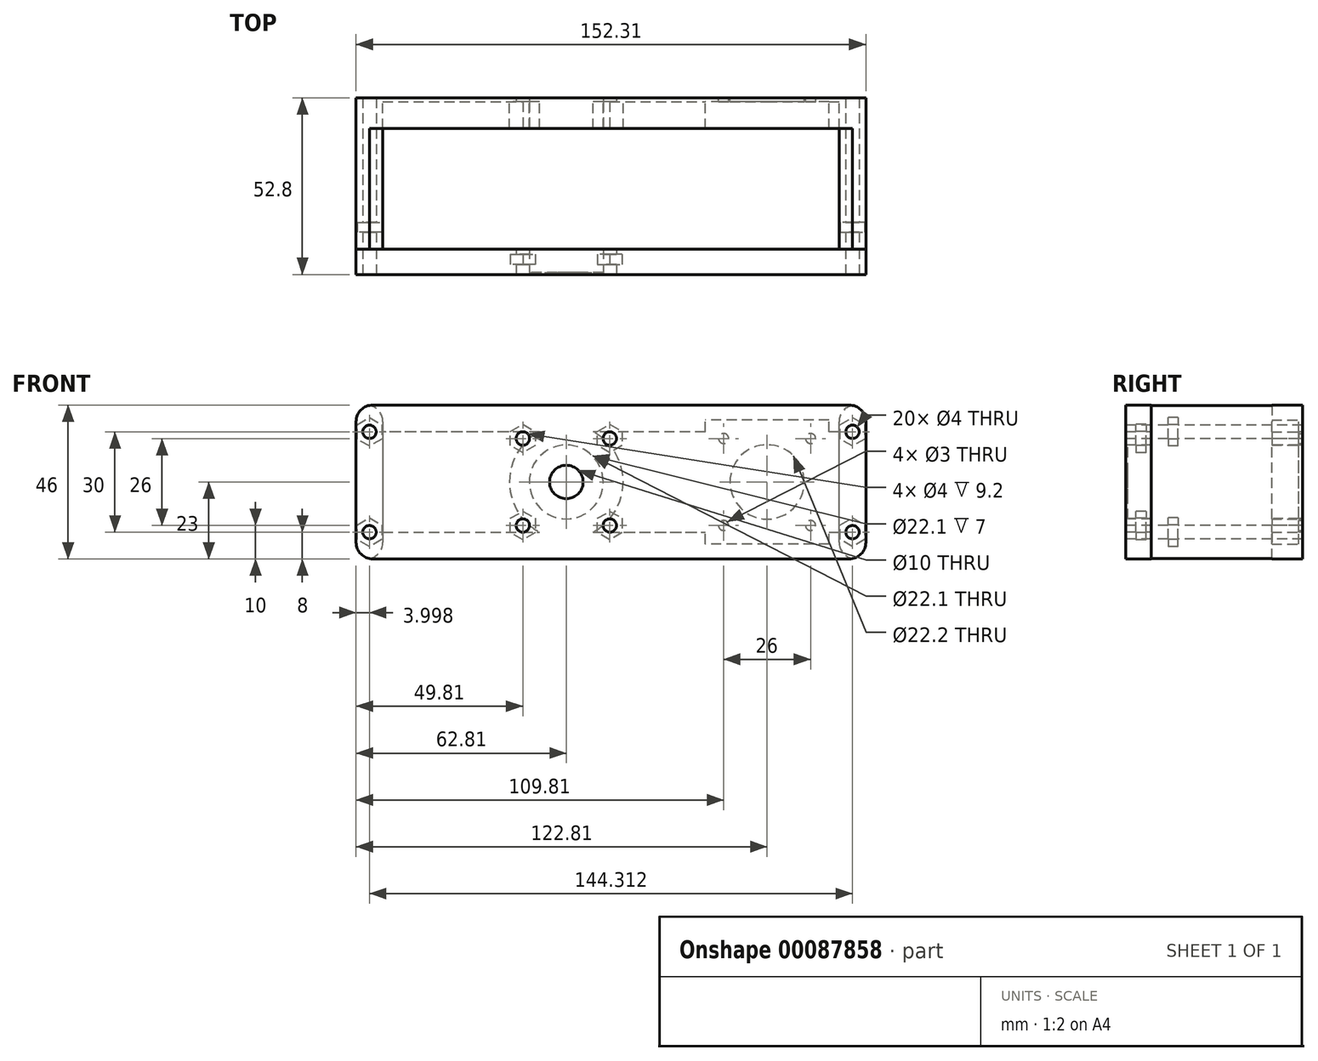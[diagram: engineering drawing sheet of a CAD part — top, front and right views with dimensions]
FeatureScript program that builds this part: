
annotation { "Feature Type Name" : "Feature", "Feature Type Description" : "" }
export const myFeature = defineFeature(function(context is Context, id is Id, definition is map)
    precondition{}
    {
        {
            var Q0;
            Q0=qCreatedBy(makeId("Front.planeOp"),FACE);
            var sketch = newSketch(context, id + "F0", { "sketchPlane" : qUnion([Q0])});
            skCircle(sketch, "E0", {"center": v(0, 0) * mm, "radius": 11.05 * mm});
            skCircle(sketch, "E1", {"center": v(60, 0) * mm, "radius": 11.1 * mm});
            skLineSegment(sketch, "E2.bottom", {"start": v(73, -13) * mm, "end": v(47, -13) * mm, "construction": true});
            skLineSegment(sketch, "E2.top", {"start": v(73, 13) * mm, "end": v(47, 13) * mm, "construction": true});
            skLineSegment(sketch, "E2.left", {"start": v(73, -13) * mm, "end": v(73, 13) * mm, "construction": true});
            skLineSegment(sketch, "E2.right", {"start": v(47, -13) * mm, "end": v(47, 13) * mm, "construction": true});
            skCircle(sketch, "E3", {"center": v(47, 13) * mm, "radius": 1.5 * mm});
            skCircle(sketch, "E4", {"center": v(73, 13) * mm, "radius": 1.5 * mm});
            skCircle(sketch, "E5", {"center": v(73, -13) * mm, "radius": 1.5 * mm});
            skCircle(sketch, "E6", {"center": v(47, -13) * mm, "radius": 1.5 * mm});
            skLineSegment(sketch, "E7.bottom", {"start": v(-62.81, 23) * mm, "end": v(89.5, 23) * mm});
            skLineSegment(sketch, "E7.top", {"start": v(-62.81, -23) * mm, "end": v(89.5, -23) * mm});
            skLineSegment(sketch, "E7.left", {"start": v(-62.81, 23) * mm, "end": v(-62.81, -23) * mm});
            skLineSegment(sketch, "E7.right", {"start": v(89.5, 23) * mm, "end": v(89.5, -23) * mm});
            skCircle(sketch, "E8", {"center": v(0, 0) * mm, "radius": 47.81 * mm, "construction": true});
            skCircle(sketch, "E9", {"center": v(60, 0) * mm, "radius": 12.19 * mm, "construction": true});
            skCircle(sketch, "E10", {"center": v(0, 0) * mm, "radius": 5 * mm});
            skSolve(sketch);
        }
        {
            var Q0;
            Q0=makeQuery(id+"F0.imprint","IMPRINT",FACE,{"disambiguationData":[TD([[makeQuery(id+"F0.imprint","IMPRINT",EDGE,{"derivedFrom":sQuery(id+"F0.wireOp",EDGE,"E0")}),-1.0]])]});
            extrude(context, id + "F1", {"entities" : qUnion([Q0]), "depth" : 1.2 * mm});
        }
        {
            var Q0;
            Q0=makeQuery(id+"F1.opExtrude","CAP_FACE",FACE,{"disambiguationData":[OSD([sQuery(id+"F0.wireOp",EDGE,"E0"),sQuery(id+"F0.wireOp",EDGE,"E1"),sQuery(id+"F0.wireOp",EDGE,"E3"),sQuery(id+"F0.wireOp",EDGE,"E4"),sQuery(id+"F0.wireOp",EDGE,"E5"),sQuery(id+"F0.wireOp",EDGE,"E6"),sQuery(id+"F0.wireOp",EDGE,"E7.bottom"),sQuery(id+"F0.wireOp",EDGE,"E7.top"),sQuery(id+"F0.wireOp",EDGE,"E7.left"),sQuery(id+"F0.wireOp",EDGE,"E7.right")])],"isStart":false});
            var sketch = newSketch(context, id + "F2", { "sketchPlane" : qUnion([Q0])});
            skLineSegment(sketch, "E11.0", {"start": v(81.5, 15) * mm, "end": v(78.5, 15) * mm});
            skLineSegment(sketch, "E11.1", {"start": v(81.5, -15) * mm, "end": v(81.5, 15) * mm});
            skLineSegment(sketch, "E11.2", {"start": v(-54.81, -15) * mm, "end": v(-8, -15) * mm});
            skLineSegment(sketch, "E11.3", {"start": v(-54.81, 15) * mm, "end": v(-54.81, -15) * mm});
            skArc(sketch, "E12", {"start": v(8, -15) * mm, "mid": v(17, 0) * mm, "end": v(8, 15) * mm});
            skLineSegment(sketch, "E13.trimOffspring", {"start": v(8, -15) * mm, "end": v(41.5, -15) * mm});
            skLineSegment(sketch, "E14.trimOffspring", {"start": v(-8, 15) * mm, "end": v(-54.81, 15) * mm});
            skArc(sketch, "E15.trimOffspring", {"start": v(-8, 15) * mm, "mid": v(-17, 0) * mm, "end": v(-8, -15) * mm});
            skLineSegment(sketch, "E16.bottom", {"start": v(78.5, -18.5) * mm, "end": v(41.5, -18.5) * mm});
            skLineSegment(sketch, "E16.top", {"start": v(78.5, 18.5) * mm, "end": v(41.5, 18.5) * mm});
            skLineSegment(sketch, "E16.left", {"start": v(78.5, -18.5) * mm, "end": v(78.5, 18.5) * mm});
            skLineSegment(sketch, "E16.right", {"start": v(41.5, -18.5) * mm, "end": v(41.5, 18.5) * mm});
            skPoint(sketch, "E16.middle", {"position": v(60, 0) * mm});
            skLineSegment(sketch, "E17.trimOffspring", {"start": v(41.5, 15) * mm, "end": v(8, 15) * mm});
            skLineSegment(sketch, "E18.trimOffspring", {"start": v(78.5, -15) * mm, "end": v(81.5, -15) * mm});
            skSolve(sketch);
        }
        {
            var Q0;
            Q0=makeQuery(id+"F2.imprint","IMPRINT",FACE,{"disambiguationData":[TD([[makeQuery(id+"F2.imprint","IMPRINT",EDGE,{"derivedFrom":sQuery(id+"F2.wireOp",EDGE,"E11.0")}),-1.0]])]});
            extrude(context, id + "F3", {"entities" : qUnion([Q0]), "operationType" : NewBodyOperationType.ADD, "depth" : 8 * mm});
        }
        {
            var Q0;
            Q0=makeQuery(id+"F3.opExtrude","CAP_FACE",FACE,{"disambiguationData":[OSD([sQuery(id+"F0.wireOp",EDGE,"E0"),sQuery(id+"F0.wireOp",EDGE,"E7.bottom"),sQuery(id+"F0.wireOp",EDGE,"E7.top"),sQuery(id+"F0.wireOp",EDGE,"E7.left"),sQuery(id+"F0.wireOp",EDGE,"E7.right"),sQuery(id+"F2.wireOp",EDGE,"E11.0"),sQuery(id+"F2.wireOp",EDGE,"E11.1"),sQuery(id+"F2.wireOp",EDGE,"E11.2"),sQuery(id+"F2.wireOp",EDGE,"E11.3"),sQuery(id+"F2.wireOp",EDGE,"E12"),sQuery(id+"F2.wireOp",EDGE,"E13.trimOffspring"),sQuery(id+"F2.wireOp",EDGE,"E14.trimOffspring"),sQuery(id+"F2.wireOp",EDGE,"E15.trimOffspring")])],"isStart":false});
            var sketch = newSketch(context, id + "F4", { "sketchPlane" : qUnion([Q0])});
            skLineSegment(sketch, "E19.bottom", {"start": v(89.5, -23) * mm, "end": v(81.5, -23) * mm});
            skLineSegment(sketch, "E19.top", {"start": v(89.5, 23) * mm, "end": v(81.5, 23) * mm});
            skLineSegment(sketch, "E19.left", {"start": v(89.5, -23) * mm, "end": v(89.5, 23) * mm});
            skLineSegment(sketch, "E19.right", {"start": v(81.5, -23) * mm, "end": v(81.5, 23) * mm});
            skLineSegment(sketch, "E20.bottom", {"start": v(-62.81, -23) * mm, "end": v(-54.81, -23) * mm});
            skLineSegment(sketch, "E20.top", {"start": v(-62.81, 23) * mm, "end": v(-54.81, 23) * mm});
            skLineSegment(sketch, "E20.left", {"start": v(-62.81, -23) * mm, "end": v(-62.81, 23) * mm});
            skLineSegment(sketch, "E20.right", {"start": v(-54.81, -23) * mm, "end": v(-54.81, 23) * mm});
            skSolve(sketch);
        }
        {
            var Q0;
            Q0 = qSketchRegion(id + "F4", true);
            extrude(context, id + "F5", {"entities" : qUnion([Q0]), "operationType" : NewBodyOperationType.ADD, "depth" : 36 * mm});
        }
        {
            var Q0;
            Q0=makeQuery(id+"F5.opExtrude","CAP_FACE",FACE,{"disambiguationData":[OSD([sQuery(id+"F4.wireOp",EDGE,"E20.bottom"),sQuery(id+"F4.wireOp",EDGE,"E20.top"),sQuery(id+"F4.wireOp",EDGE,"E20.left"),sQuery(id+"F4.wireOp",EDGE,"E20.right")])],"isStart":false});
            var sketch = newSketch(context, id + "F6", { "sketchPlane" : qUnion([Q0])});
            skLineSegment(sketch, "E21.0.2", {"start": v(89.5, -23) * mm, "end": v(89.5, 23) * mm});
            skLineSegment(sketch, "E22.0", {"start": v(-62.81, 23) * mm, "end": v(-62.81, -23) * mm});
            skLineSegment(sketch, "E23", {"start": v(-62.81, -23) * mm, "end": v(89.5, -23) * mm});
            skLineSegment(sketch, "E24", {"start": v(-62.81, 23) * mm, "end": v(89.5, 23) * mm});
            skSolve(sketch);
        }
        {
            var Q0;
            Q0 = qSketchRegion(id + "F6", true);
            extrude(context, id + "F7", {"entities" : qUnion([Q0]), "depth" : 7.6 * mm});
        }
        {
            var Q0;
            Q0=makeQuery(id+"F0.imprint","IMPRINT",FACE,{"disambiguationData":[TD([[makeQuery(id+"F0.imprint","IMPRINT",EDGE,{"derivedFrom":sQuery(id+"F0.wireOp",EDGE,"E0")}),1.0]])]});
            extrude(context, id + "F8", {"entities" : qUnion([Q0]), "operationType" : NewBodyOperationType.ADD, "depth" : .6 * mm});
        }
        {
            var Q0;
            Q0=makeQuery(id+"F7.opExtrude","CAP_FACE",FACE,{"disambiguationData":[OSD([sQuery(id+"F6.wireOp",EDGE,"E21.0.2"),sQuery(id+"F6.wireOp",EDGE,"E22.0"),sQuery(id+"F6.wireOp",EDGE,"E23"),sQuery(id+"F6.wireOp",EDGE,"E24")])],"isStart":false});
            var sketch = newSketch(context, id + "F9", { "sketchPlane" : qUnion([Q0])});
            skCircle(sketch, "E25.0", {"center": v(0, 0) * mm, "radius": 11.05 * mm});
            skCircle(sketch, "E26.0", {"center": v(0, 0) * mm, "radius": 5 * mm});
            skLineSegment(sketch, "E27.bottom", {"start": v(13, -13) * mm, "end": v(-13, -13) * mm, "construction": true});
            skLineSegment(sketch, "E27.top", {"start": v(13, 13) * mm, "end": v(-13, 13) * mm, "construction": true});
            skLineSegment(sketch, "E27.left", {"start": v(13, -13) * mm, "end": v(13, 13) * mm, "construction": true});
            skLineSegment(sketch, "E27.right", {"start": v(-13, -13) * mm, "end": v(-13, 13) * mm, "construction": true});
            skCircle(sketch, "E28", {"center": v(-13, -13) * mm, "radius": 2 * mm});
            skCircle(sketch, "E29", {"center": v(13, -13) * mm, "radius": 2 * mm});
            skCircle(sketch, "E30", {"center": v(13, 13) * mm, "radius": 2 * mm});
            skCircle(sketch, "E31", {"center": v(-13, 13) * mm, "radius": 2 * mm});
            skSolve(sketch);
        }
        {
            var Q0;
            Q0 = qSketchRegion(id + "F9", true);
            var Q1;
            Q1=makeQuery(id+"F9.imprint","IMPRINT",FACE,{"disambiguationData":[TD([[makeQuery(id+"F9.imprint","IMPRINT",EDGE,{"derivedFrom":sQuery(id+"F9.wireOp",EDGE,"E25.0")}),1.0]])]});
            var Q2;
            Q2=makeQuery(id+"F9.imprint","IMPRINT",FACE,{"disambiguationData":[TD([[makeQuery(id+"F9.imprint","IMPRINT",EDGE,{"derivedFrom":sQuery(id+"F9.wireOp",EDGE,"E26.0")}),1.0]])]});
            extrude(context, id + "F10", {"entities" : qUnion([Q0, Q1, Q2]), "operationType" : NewBodyOperationType.REMOVE, "endBound" : BoundingType.THROUGH_ALL, "oppositeDirection" : true, "depth" : 25 * mm});
        }
        {
            var Q0;
            Q0=makeQuery(id+"F9.imprint","IMPRINT",FACE,{"disambiguationData":[TD([[makeQuery(id+"F9.imprint","IMPRINT",EDGE,{"derivedFrom":sQuery(id+"F9.wireOp",EDGE,"E25.0")}),1.0]])]});
            extrude(context, id + "F11", {"entities" : qUnion([Q0]), "operationType" : NewBodyOperationType.ADD, "oppositeDirection" : true, "depth" : .6 * mm});
        }
        {
            var Q0;
            Q0=makeQuery(id+"F9.imprint","IMPRINT",FACE,{"disambiguationData":[TD([[makeQuery(id+"F9.imprint","IMPRINT",EDGE,{"derivedFrom":sQuery(id+"F9.wireOp",EDGE,"E25.0")}),-1.0]])]});
            cPlane(context, id + "F12", {"entities" : qUnion([Q0]), "cplaneType" : CPlaneType.OFFSET, "offset" : 3 * mm, "oppositeDirection" : true, "width" : 150 * mm, "height" : 150 * mm});
        }
        {
            var Q0;
            Q0=qCreatedBy(id+"F12.planeOp",FACE);
            var sketch = newSketch(context, id + "F13", { "sketchPlane" : qUnion([Q0])});
            skLineSegment(sketch, "E32.0", {"start": v(13, -13) * mm, "end": v(-13, -13) * mm, "construction": true});
            skLineSegment(sketch, "E33.0", {"start": v(-13, -13) * mm, "end": v(-13, 13) * mm, "construction": true});
            skLineSegment(sketch, "E34.0", {"start": v(13, 13) * mm, "end": v(-13, 13) * mm, "construction": true});
            skLineSegment(sketch, "E35.0", {"start": v(13, -13) * mm, "end": v(13, 13) * mm, "construction": true});
            skCircle(sketch, "E36.cCircle", {"center": v(-13, -13) * mm, "radius": 3.7 * mm, "construction": true});
            skLineSegment(sketch, "E36.0", {"start": v(-9.3, -10.86) * mm, "end": v(-9.3, -15.14) * mm});
            skLineSegment(sketch, "E36.1", {"start": v(-9.3, -15.14) * mm, "end": v(-13, -17.27) * mm});
            skLineSegment(sketch, "E36.2", {"start": v(-13, -17.27) * mm, "end": v(-16.7, -15.14) * mm});
            skLineSegment(sketch, "E36.3", {"start": v(-16.7, -15.14) * mm, "end": v(-16.7, -10.86) * mm});
            skLineSegment(sketch, "E36.4", {"start": v(-16.7, -10.86) * mm, "end": v(-13, -8.73) * mm});
            skLineSegment(sketch, "E36.5", {"start": v(-13, -8.73) * mm, "end": v(-9.3, -10.86) * mm});
            skPoint(sketch, "E36.0.midPoint", {"position": v(-9.3, -13) * mm});
            skCircle(sketch, "E37.cCircle", {"center": v(-13, 13) * mm, "radius": 3.7 * mm, "construction": true});
            skLineSegment(sketch, "E37.0", {"start": v(-9.3, 15.14) * mm, "end": v(-9.3, 10.86) * mm});
            skLineSegment(sketch, "E37.1", {"start": v(-9.3, 10.86) * mm, "end": v(-13, 8.73) * mm});
            skLineSegment(sketch, "E37.2", {"start": v(-13, 8.73) * mm, "end": v(-16.7, 10.86) * mm});
            skLineSegment(sketch, "E37.3", {"start": v(-16.7, 10.86) * mm, "end": v(-16.7, 15.14) * mm});
            skLineSegment(sketch, "E37.4", {"start": v(-16.7, 15.14) * mm, "end": v(-13, 17.27) * mm});
            skLineSegment(sketch, "E37.5", {"start": v(-13, 17.27) * mm, "end": v(-9.3, 15.14) * mm});
            skPoint(sketch, "E37.0.midPoint", {"position": v(-9.3, 13) * mm});
            skCircle(sketch, "E38.cCircle", {"center": v(13, 13) * mm, "radius": 3.7 * mm, "construction": true});
            skLineSegment(sketch, "E38.0", {"start": v(9.3, 10.86) * mm, "end": v(9.3, 15.14) * mm});
            skLineSegment(sketch, "E38.1", {"start": v(9.3, 15.14) * mm, "end": v(13, 17.27) * mm});
            skLineSegment(sketch, "E38.2", {"start": v(13, 17.27) * mm, "end": v(16.7, 15.14) * mm});
            skLineSegment(sketch, "E38.3", {"start": v(16.7, 15.14) * mm, "end": v(16.7, 10.86) * mm});
            skLineSegment(sketch, "E38.4", {"start": v(16.7, 10.86) * mm, "end": v(13, 8.73) * mm});
            skLineSegment(sketch, "E38.5", {"start": v(13, 8.73) * mm, "end": v(9.3, 10.86) * mm});
            skPoint(sketch, "E38.0.midPoint", {"position": v(9.3, 13) * mm});
            skCircle(sketch, "E39.cCircle", {"center": v(13, -13) * mm, "radius": 3.7 * mm, "construction": true});
            skLineSegment(sketch, "E39.0", {"start": v(9.3, -15.14) * mm, "end": v(9.3, -10.86) * mm});
            skLineSegment(sketch, "E39.1", {"start": v(9.3, -10.86) * mm, "end": v(13, -8.73) * mm});
            skLineSegment(sketch, "E39.2", {"start": v(13, -8.73) * mm, "end": v(16.7, -10.86) * mm});
            skLineSegment(sketch, "E39.3", {"start": v(16.7, -10.86) * mm, "end": v(16.7, -15.14) * mm});
            skLineSegment(sketch, "E39.4", {"start": v(16.7, -15.14) * mm, "end": v(13, -17.27) * mm});
            skLineSegment(sketch, "E39.5", {"start": v(13, -17.27) * mm, "end": v(9.3, -15.14) * mm});
            skPoint(sketch, "E39.0.midPoint", {"position": v(9.3, -13) * mm});
            skSolve(sketch);
        }
        {
            var Q0;
            Q0 = qSketchRegion(id + "F13", true);
            extrude(context, id + "F14", {"entities" : qUnion([Q0]), "operationType" : NewBodyOperationType.REMOVE, "oppositeDirection" : true, "depth" : 3 * mm});
        }
        {
            var Q0;
            Q0=makeQuery(id+"F5.opExtrude","CAP_FACE",FACE,{"disambiguationData":[OSD([sQuery(id+"F4.wireOp",EDGE,"E20.bottom"),sQuery(id+"F4.wireOp",EDGE,"E20.top"),sQuery(id+"F4.wireOp",EDGE,"E20.left"),sQuery(id+"F4.wireOp",EDGE,"E20.right")])],"isStart":false});
            var sketch = newSketch(context, id + "F15", { "sketchPlane" : qUnion([Q0])});
            skLineSegment(sketch, "E40.0.0", {"start": v(81.5, 23) * mm, "end": v(81.5, -23) * mm, "construction": true});
            skLineSegment(sketch, "E40.0.1", {"start": v(81.5, -23) * mm, "end": v(89.5, -23) * mm, "construction": true});
            skLineSegment(sketch, "E40.0.2", {"start": v(89.5, -23) * mm, "end": v(89.5, 23) * mm, "construction": true});
            skLineSegment(sketch, "E40.0.3", {"start": v(89.5, 23) * mm, "end": v(81.5, 23) * mm, "construction": true});
            skLineSegment(sketch, "E41", {"start": v(-58.81, -23) * mm, "end": v(-58.81, 23) * mm, "construction": true});
            skLineSegment(sketch, "E42", {"start": v(85.5, -23) * mm, "end": v(85.5, 23) * mm, "construction": true});
            skCircle(sketch, "E43", {"center": v(85.5, 15) * mm, "radius": 2 * mm});
            skCircle(sketch, "E44", {"center": v(85.5, -15) * mm, "radius": 2 * mm});
            skCircle(sketch, "E45", {"center": v(-58.81, 15) * mm, "radius": 2 * mm});
            skCircle(sketch, "E46", {"center": v(-58.81, -15) * mm, "radius": 2 * mm});
            skSolve(sketch);
        }
        {
            var Q0;
            Q0 = qSketchRegion(id + "F15", true);
            extrude(context, id + "F16", {"entities" : qUnion([Q0]), "operationType" : NewBodyOperationType.REMOVE, "oppositeDirection" : true, "depth" : 15 * mm});
        }
        {
            var Q0;
            Q0=makeQuery(id+"F15.imprint","IMPRINT",FACE,{"disambiguationData":[TD([[makeQuery(id+"F15.imprint","IMPRINT",EDGE,{"derivedFrom":sQuery(id+"F15.wireOp",EDGE,"E45")}),-1.0]])]});
            cPlane(context, id + "F17", {"entities" : qUnion([Q0]), "cplaneType" : CPlaneType.OFFSET, "offset" : 5 * mm, "oppositeDirection" : true, "width" : 150 * mm, "height" : 150 * mm});
        }
        {
            var Q0;
            Q0=qCreatedBy(id+"F17.planeOp",FACE);
            var sketch = newSketch(context, id + "F18", { "sketchPlane" : qUnion([Q0])});
            skPoint(sketch, "E47.0", {"position": v(-58.81, -15) * mm});
            skPoint(sketch, "E48.0", {"position": v(-58.81, 15) * mm});
            skPoint(sketch, "E49.0", {"position": v(85.5, -15) * mm});
            skPoint(sketch, "E50.0", {"position": v(85.5, 15) * mm});
            skCircle(sketch, "E51.cCircle", {"center": v(-58.81, 15) * mm, "radius": 3.7 * mm, "construction": true});
            skLineSegment(sketch, "E51.0", {"start": v(-55.11, 17.14) * mm, "end": v(-55.11, 12.86) * mm});
            skLineSegment(sketch, "E51.1", {"start": v(-55.11, 12.86) * mm, "end": v(-58.81, 10.73) * mm});
            skLineSegment(sketch, "E51.2", {"start": v(-58.81, 10.73) * mm, "end": v(-62.51, 12.86) * mm});
            skLineSegment(sketch, "E51.3", {"start": v(-62.51, 12.86) * mm, "end": v(-62.51, 17.14) * mm});
            skLineSegment(sketch, "E51.4", {"start": v(-62.51, 17.14) * mm, "end": v(-58.81, 19.27) * mm});
            skLineSegment(sketch, "E51.5", {"start": v(-58.81, 19.27) * mm, "end": v(-55.11, 17.14) * mm});
            skPoint(sketch, "E51.0.midPoint", {"position": v(-55.11, 15) * mm});
            skCircle(sketch, "E52.cCircle", {"center": v(-58.81, -15) * mm, "radius": 3.7 * mm, "construction": true});
            skLineSegment(sketch, "E52.0", {"start": v(-55.11, -12.86) * mm, "end": v(-55.11, -17.14) * mm});
            skLineSegment(sketch, "E52.1", {"start": v(-55.11, -17.14) * mm, "end": v(-58.81, -19.27) * mm});
            skLineSegment(sketch, "E52.2", {"start": v(-58.81, -19.27) * mm, "end": v(-62.51, -17.14) * mm});
            skLineSegment(sketch, "E52.3", {"start": v(-62.51, -17.14) * mm, "end": v(-62.51, -12.86) * mm});
            skLineSegment(sketch, "E52.4", {"start": v(-62.51, -12.86) * mm, "end": v(-58.81, -10.73) * mm});
            skLineSegment(sketch, "E52.5", {"start": v(-58.81, -10.73) * mm, "end": v(-55.11, -12.86) * mm});
            skPoint(sketch, "E52.0.midPoint", {"position": v(-55.11, -15) * mm});
            skCircle(sketch, "E53.cCircle", {"center": v(85.5, 15) * mm, "radius": 3.7 * mm, "construction": true});
            skLineSegment(sketch, "E53.0", {"start": v(81.8, 12.86) * mm, "end": v(81.8, 17.14) * mm});
            skLineSegment(sketch, "E53.1", {"start": v(81.8, 17.14) * mm, "end": v(85.5, 19.27) * mm});
            skLineSegment(sketch, "E53.2", {"start": v(85.5, 19.27) * mm, "end": v(89.2, 17.14) * mm});
            skLineSegment(sketch, "E53.3", {"start": v(89.2, 17.14) * mm, "end": v(89.2, 12.86) * mm});
            skLineSegment(sketch, "E53.4", {"start": v(89.2, 12.86) * mm, "end": v(85.5, 10.73) * mm});
            skLineSegment(sketch, "E53.5", {"start": v(85.5, 10.73) * mm, "end": v(81.8, 12.86) * mm});
            skPoint(sketch, "E53.0.midPoint", {"position": v(81.8, 15) * mm});
            skCircle(sketch, "E54.cCircle", {"center": v(85.5, -15) * mm, "radius": 3.7 * mm, "construction": true});
            skLineSegment(sketch, "E54.0", {"start": v(81.8, -17.14) * mm, "end": v(81.8, -12.86) * mm});
            skLineSegment(sketch, "E54.1", {"start": v(81.8, -12.86) * mm, "end": v(85.5, -10.73) * mm});
            skLineSegment(sketch, "E54.2", {"start": v(85.5, -10.73) * mm, "end": v(89.2, -12.86) * mm});
            skLineSegment(sketch, "E54.3", {"start": v(89.2, -12.86) * mm, "end": v(89.2, -17.14) * mm});
            skLineSegment(sketch, "E54.4", {"start": v(89.2, -17.14) * mm, "end": v(85.5, -19.27) * mm});
            skLineSegment(sketch, "E54.5", {"start": v(85.5, -19.27) * mm, "end": v(81.8, -17.14) * mm});
            skPoint(sketch, "E54.0.midPoint", {"position": v(81.8, -15) * mm});
            skSolve(sketch);
        }
        {
            var Q0;
            Q0 = qSketchRegion(id + "F18", true);
            extrude(context, id + "F19", {"entities" : qUnion([Q0]), "operationType" : NewBodyOperationType.REMOVE, "oppositeDirection" : true, "depth" : 3 * mm});
        }
        {
            var Q0;
            Q0=makeQuery(id+"F11.boolean.opBoolean","MERGE",FACE,{"derivedFrom":[makeQuery(id+"F7.opExtrude","CAP_FACE",FACE,{"disambiguationData":[OSD([sQuery(id+"F6.wireOp",EDGE,"E21.0.2"),sQuery(id+"F6.wireOp",EDGE,"E22.0"),sQuery(id+"F6.wireOp",EDGE,"E23"),sQuery(id+"F6.wireOp",EDGE,"E24")])],"isStart":false}),makeQuery(id+"F11.opExtrude","CAP_FACE",FACE,{"disambiguationData":[OSD([sQuery(id+"F9.wireOp",EDGE,"E25.0"),sQuery(id+"F9.wireOp",EDGE,"E26.0")])],"isStart":true})]});
            var sketch = newSketch(context, id + "F20", { "sketchPlane" : qUnion([Q0])});
            skCircle(sketch, "E55.0", {"center": v(-58.81, -15) * mm, "radius": 2 * mm});
            skCircle(sketch, "E56.0", {"center": v(-58.81, 15) * mm, "radius": 2 * mm});
            skCircle(sketch, "E57.0", {"center": v(85.5, 15) * mm, "radius": 2 * mm});
            skCircle(sketch, "E58.0", {"center": v(85.5, -15) * mm, "radius": 2 * mm});
            skSolve(sketch);
        }
        {
            var Q0;
            Q0 = qSketchRegion(id + "F20", true);
            extrude(context, id + "F21", {"entities" : qUnion([Q0]), "operationType" : NewBodyOperationType.REMOVE, "endBound" : BoundingType.THROUGH_ALL, "oppositeDirection" : true, "depth" : 25 * mm});
        }
        {
            var Q0;
            {var subQ0=sQuery(id+"F0.wireOp",EDGE,"E7.left");var subQ1=sQuery(id+"F0.wireOp",EDGE,"E7.top");Q0=makeQuery(id+"F5.boolean.opBoolean","MERGE",EDGE,{"derivedFrom":[makeQuery(id+"F3.boolean.opBoolean","MERGE",EDGE,{"derivedFrom":[makeQuery(id+"F1.opExtrude","SWEPT_EDGE",EDGE,{"disambiguationData":[OSD([subQ1,subQ0])]}),makeQuery(id+"F3.opExtrude","SWEPT_EDGE",EDGE,{"disambiguationData":[OSD([subQ1,subQ0])]})]}),makeQuery(id+"F5.opExtrude","SWEPT_EDGE",EDGE,{"disambiguationData":[OSD([sQuery(id+"F4.wireOp",EDGE,"E20.bottom"),sQuery(id+"F4.wireOp",EDGE,"E20.left")])]})]});}
            var Q1;
            Q1=makeQuery(id+"F7.opExtrude","SWEPT_EDGE",EDGE,{"disambiguationData":[OSD([sQuery(id+"F6.wireOp",EDGE,"E22.0"),sQuery(id+"F6.wireOp",EDGE,"E23")])]});
            var Q2;
            Q2=makeQuery(id+"F7.opExtrude","SWEPT_EDGE",EDGE,{"disambiguationData":[OSD([sQuery(id+"F6.wireOp",EDGE,"E22.0"),sQuery(id+"F6.wireOp",EDGE,"E24")])]});
            var Q3;
            {var subQ0=sQuery(id+"F0.wireOp",EDGE,"E7.left");var subQ1=sQuery(id+"F0.wireOp",EDGE,"E7.bottom");Q3=makeQuery(id+"F5.boolean.opBoolean","MERGE",EDGE,{"derivedFrom":[makeQuery(id+"F3.boolean.opBoolean","MERGE",EDGE,{"derivedFrom":[makeQuery(id+"F1.opExtrude","SWEPT_EDGE",EDGE,{"disambiguationData":[OSD([subQ1,subQ0])]}),makeQuery(id+"F3.opExtrude","SWEPT_EDGE",EDGE,{"disambiguationData":[OSD([subQ1,subQ0])]})]}),makeQuery(id+"F5.opExtrude","SWEPT_EDGE",EDGE,{"disambiguationData":[OSD([sQuery(id+"F4.wireOp",EDGE,"E20.top"),sQuery(id+"F4.wireOp",EDGE,"E20.left")])]})]});}
            var Q4;
            Q4=makeQuery(id+"F5.opExtrude","SWEPT_EDGE",EDGE,{"disambiguationData":[OSD([sQuery(id+"F0.wireOp",EDGE,"E7.bottom"),sQuery(id+"F4.wireOp",EDGE,"E20.top"),sQuery(id+"F4.wireOp",EDGE,"E20.right")])]});
            var Q5;
            Q5=makeQuery(id+"F5.opExtrude","SWEPT_EDGE",EDGE,{"disambiguationData":[OSD([sQuery(id+"F0.wireOp",EDGE,"E7.top"),sQuery(id+"F4.wireOp",EDGE,"E20.bottom"),sQuery(id+"F4.wireOp",EDGE,"E20.right")])]});
            var Q6;
            Q6=makeQuery(id+"F5.opExtrude","SWEPT_EDGE",EDGE,{"disambiguationData":[OSD([sQuery(id+"F0.wireOp",EDGE,"E7.top"),sQuery(id+"F4.wireOp",EDGE,"E19.bottom"),sQuery(id+"F4.wireOp",EDGE,"E19.right")])]});
            var Q7;
            {var subQ0=sQuery(id+"F0.wireOp",EDGE,"E7.right");var subQ1=sQuery(id+"F0.wireOp",EDGE,"E7.top");Q7=makeQuery(id+"F5.boolean.opBoolean","MERGE",EDGE,{"derivedFrom":[makeQuery(id+"F3.boolean.opBoolean","MERGE",EDGE,{"derivedFrom":[makeQuery(id+"F1.opExtrude","SWEPT_EDGE",EDGE,{"disambiguationData":[OSD([subQ1,subQ0])]}),makeQuery(id+"F3.opExtrude","SWEPT_EDGE",EDGE,{"disambiguationData":[OSD([subQ1,subQ0])]})]}),makeQuery(id+"F5.opExtrude","SWEPT_EDGE",EDGE,{"disambiguationData":[OSD([sQuery(id+"F4.wireOp",EDGE,"E19.bottom"),sQuery(id+"F4.wireOp",EDGE,"E19.left")])]})]});}
            var Q8;
            Q8=makeQuery(id+"F7.opExtrude","SWEPT_EDGE",EDGE,{"disambiguationData":[OSD([sQuery(id+"F6.wireOp",EDGE,"E21.0.2"),sQuery(id+"F6.wireOp",EDGE,"E23")])]});
            var Q9;
            {var subQ0=sQuery(id+"F0.wireOp",EDGE,"E7.right");var subQ1=sQuery(id+"F0.wireOp",EDGE,"E7.bottom");Q9=makeQuery(id+"F5.boolean.opBoolean","MERGE",EDGE,{"derivedFrom":[makeQuery(id+"F3.boolean.opBoolean","MERGE",EDGE,{"derivedFrom":[makeQuery(id+"F1.opExtrude","SWEPT_EDGE",EDGE,{"disambiguationData":[OSD([subQ1,subQ0])]}),makeQuery(id+"F3.opExtrude","SWEPT_EDGE",EDGE,{"disambiguationData":[OSD([subQ1,subQ0])]})]}),makeQuery(id+"F5.opExtrude","SWEPT_EDGE",EDGE,{"disambiguationData":[OSD([sQuery(id+"F4.wireOp",EDGE,"E19.top"),sQuery(id+"F4.wireOp",EDGE,"E19.left")])]})]});}
            var Q10;
            Q10=makeQuery(id+"F7.opExtrude","SWEPT_EDGE",EDGE,{"disambiguationData":[OSD([sQuery(id+"F6.wireOp",EDGE,"E21.0.2"),sQuery(id+"F6.wireOp",EDGE,"E24")])]});
            var Q11;
            Q11=makeQuery(id+"F5.opExtrude","SWEPT_EDGE",EDGE,{"disambiguationData":[OSD([sQuery(id+"F0.wireOp",EDGE,"E7.bottom"),sQuery(id+"F4.wireOp",EDGE,"E19.top"),sQuery(id+"F4.wireOp",EDGE,"E19.right")])]});
            fillet(context, id + "F22", {"entities" : qUnion([Q0, Q1, Q2, Q3, Q4, Q5, Q6, Q7, Q8, Q9, Q10, Q11]), "radius" : 5 * mm, "tangentPropagation" : true, "allowEdgeOverflow" : false});
        }
    });
